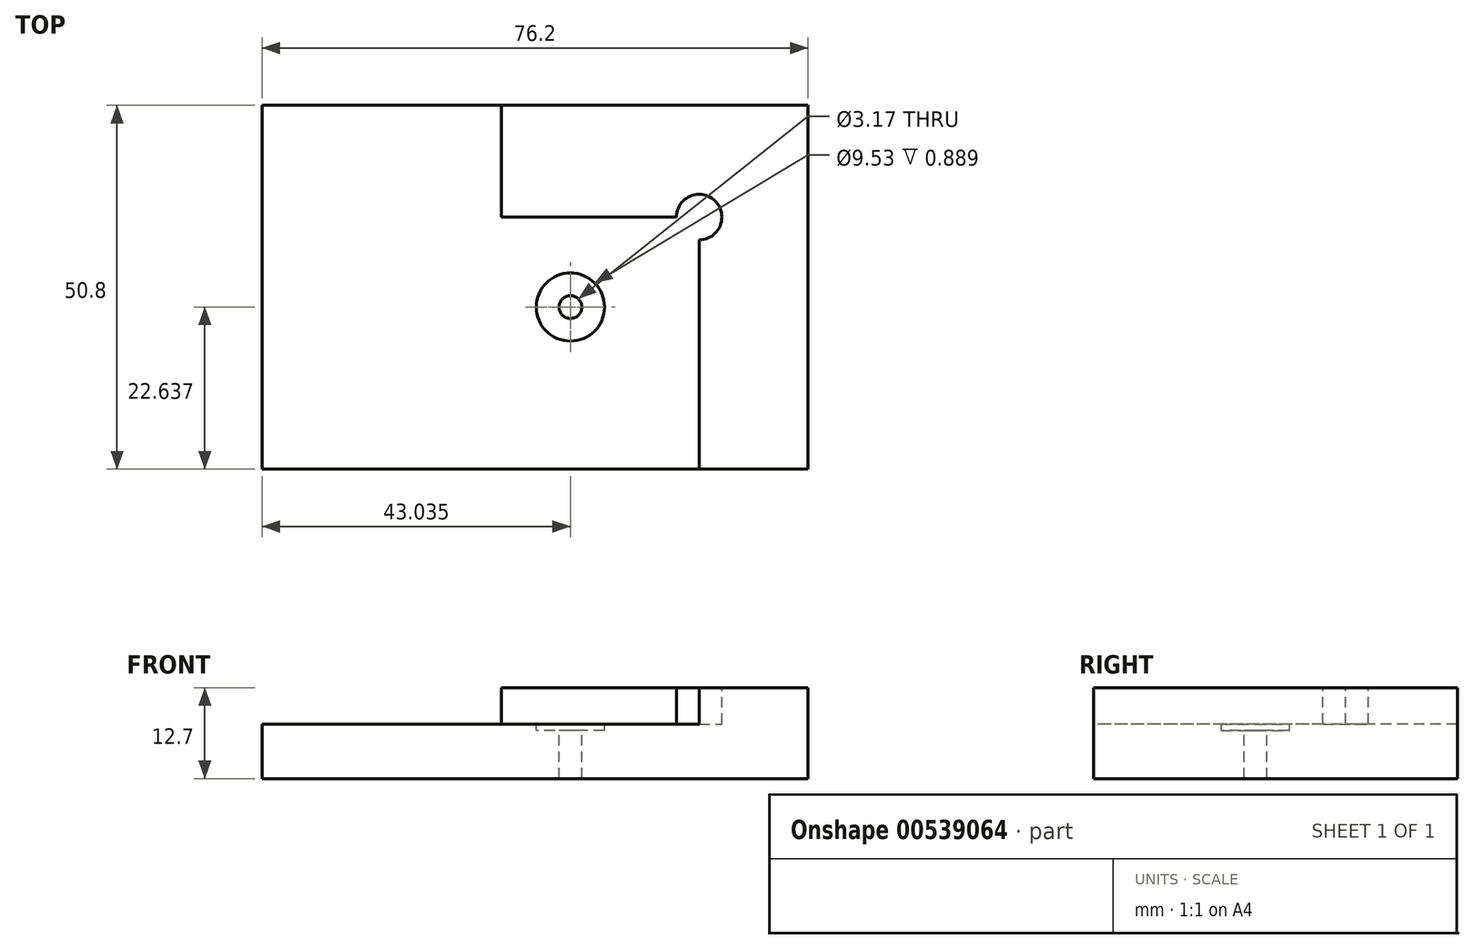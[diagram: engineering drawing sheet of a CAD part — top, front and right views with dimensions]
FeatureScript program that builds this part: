
annotation { "Feature Type Name" : "Feature", "Feature Type Description" : "" }
export const myFeature = defineFeature(function(context is Context, id is Id, definition is map)
    precondition{}
    {
        {
            var Q0;
            Q0=qCreatedBy(makeId("Top.planeOp"),FACE);
            var sketch = newSketch(context, id + "F0", { "sketchPlane" : qUnion([Q0])});
            skLineSegment(sketch, "E0.bottom", {"start": v(-36.33, 24.69) * mm, "end": v(39.87, 24.69) * mm});
            skLineSegment(sketch, "E0.top", {"start": v(-36.33, -26.11) * mm, "end": v(39.87, -26.11) * mm});
            skLineSegment(sketch, "E0.left", {"start": v(-36.33, 24.69) * mm, "end": v(-36.33, -26.11) * mm});
            skLineSegment(sketch, "E0.right", {"start": v(39.87, 24.69) * mm, "end": v(39.87, -26.11) * mm});
            skSolve(sketch);
        }
        {
            var Q0;
            Q0 = qSketchRegion(id + "F0", true);
            extrude(context, id + "F1", {"entities" : qUnion([Q0]), "depth" : 12.7 * mm, "offsetDistance" : 25.4 * mm});
        }
        {
            var Q0;
            Q0=makeQuery(id+"F1.opExtrude","CAP_FACE",FACE,{"disambiguationData":[OSD([sQuery(id+"F0.wireOp",EDGE,"E0.bottom"),sQuery(id+"F0.wireOp",EDGE,"E0.top"),sQuery(id+"F0.wireOp",EDGE,"E0.left"),sQuery(id+"F0.wireOp",EDGE,"E0.right")])],"isStart":false});
            var sketch = newSketch(context, id + "F2", { "sketchPlane" : qUnion([Q0])});
            skLineSegment(sketch, "E1", {"start": v(-2.96, 24.69) * mm, "end": v(-2.96, 9.09) * mm});
            skLineSegment(sketch, "E2", {"start": v(-2.96, 9.09) * mm, "end": v(21.5, 9.09) * mm});
            skLineSegment(sketch, "E3", {"start": v(24.68, 5.91) * mm, "end": v(24.68, -26.11) * mm});
            skLineSegment(sketch, "E4", {"start": v(24.68, -26.11) * mm, "end": v(-36.33, -26.11) * mm});
            skLineSegment(sketch, "E5", {"start": v(-36.33, -26.11) * mm, "end": v(-36.33, 24.69) * mm});
            skLineSegment(sketch, "E6", {"start": v(-36.33, 24.69) * mm, "end": v(-2.96, 24.69) * mm});
            skArc(sketch, "E7", {"start": v(24.68, 5.91) * mm, "mid": v(26.92, 11.33) * mm, "end": v(21.5, 9.09) * mm});
            skSolve(sketch);
        }
        {
            var Q0;
            Q0 = qSketchRegion(id + "F2", true);
            extrude(context, id + "F3", {"entities" : qUnion([Q0]), "operationType" : NewBodyOperationType.REMOVE, "oppositeDirection" : true, "depth" : 5.08 * mm, "offsetDistance" : 25.4 * mm});
        }
        {
            var Q0;
            Q0=makeQuery(id+"F3.boolean.opBoolean","COPY",FACE,{"derivedFrom":makeQuery(id+"F3.opExtrude","CAP_FACE",FACE,{"disambiguationData":[OSD([sQuery(id+"F2.wireOp",EDGE,"E1"),sQuery(id+"F2.wireOp",EDGE,"E2"),sQuery(id+"F2.wireOp",EDGE,"E3"),sQuery(id+"F2.wireOp",EDGE,"E4"),sQuery(id+"F2.wireOp",EDGE,"E5"),sQuery(id+"F2.wireOp",EDGE,"E6"),sQuery(id+"F2.wireOp",EDGE,"E7")])],"isStart":false})});
            var sketch = newSketch(context, id + "F4", { "sketchPlane" : qUnion([Q0])});
            skCircle(sketch, "E8", {"center": v(6.7, -3.47) * mm, "radius": 1.59 * mm});
            skSolve(sketch);
        }
        {
            var Q0;
            Q0 = qSketchRegion(id + "F4", true);
            extrude(context, id + "F5", {"entities" : qUnion([Q0]), "operationType" : NewBodyOperationType.REMOVE, "oppositeDirection" : true, "depth" : 25.4 * mm, "offsetDistance" : 25.4 * mm});
        }
        {
            var Q0;
            Q0=makeQuery(id+"F3.boolean.opBoolean","COPY",FACE,{"derivedFrom":makeQuery(id+"F3.opExtrude","CAP_FACE",FACE,{"disambiguationData":[OSD([sQuery(id+"F2.wireOp",EDGE,"E1"),sQuery(id+"F2.wireOp",EDGE,"E2"),sQuery(id+"F2.wireOp",EDGE,"E3"),sQuery(id+"F2.wireOp",EDGE,"E4"),sQuery(id+"F2.wireOp",EDGE,"E5"),sQuery(id+"F2.wireOp",EDGE,"E6"),sQuery(id+"F2.wireOp",EDGE,"E7")])],"isStart":false})});
            var sketch = newSketch(context, id + "F6", { "sketchPlane" : qUnion([Q0])});
            skCircle(sketch, "E9", {"center": v(6.7, -3.47) * mm, "radius": 4.76 * mm});
            skSolve(sketch);
        }
        {
            var Q0;
            Q0 = qSketchRegion(id + "F6", true);
            extrude(context, id + "F7", {"entities" : qUnion([Q0]), "operationType" : NewBodyOperationType.REMOVE, "oppositeDirection" : true, "depth" : 0.89 * mm, "offsetDistance" : 25.4 * mm});
        }
    });
